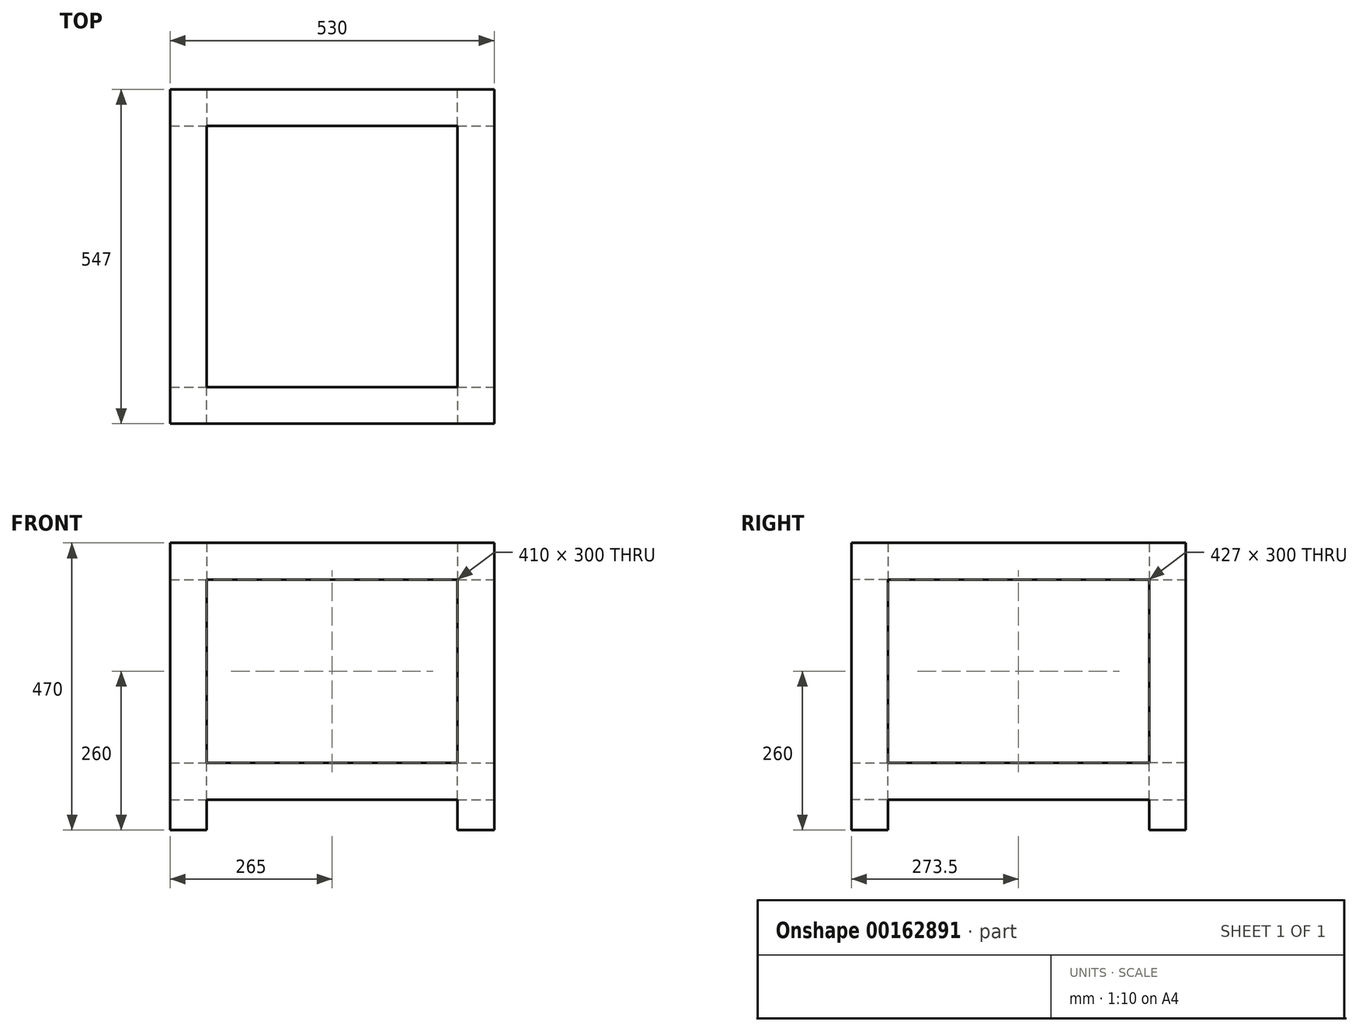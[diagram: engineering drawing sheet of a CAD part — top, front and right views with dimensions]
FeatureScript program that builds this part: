
annotation { "Feature Type Name" : "Feature", "Feature Type Description" : "" }
export const myFeature = defineFeature(function(context is Context, id is Id, definition is map)
    precondition{}
    {
        {
            var Q0;
            Q0=qCreatedBy(makeId("Top.planeOp"),FACE);
            var sketch = newSketch(context, id + "F0", { "sketchPlane" : qUnion([Q0])});
            skLineSegment(sketch, "E0.bottom", {"start": v(205, -213.5) * mm, "end": v(-205, -213.5) * mm});
            skLineSegment(sketch, "E0.top", {"start": v(205, 213.5) * mm, "end": v(-205, 213.5) * mm});
            skLineSegment(sketch, "E0.left", {"start": v(205, -213.5) * mm, "end": v(205, 213.5) * mm});
            skLineSegment(sketch, "E0.right", {"start": v(-205, -213.5) * mm, "end": v(-205, 213.5) * mm});
            skPoint(sketch, "E0.middle", {"position": v(0, 0) * mm});
            skLineSegment(sketch, "E1.bottom", {"start": v(265, -273.5) * mm, "end": v(-265, -273.5) * mm});
            skLineSegment(sketch, "E1.top", {"start": v(265, 273.5) * mm, "end": v(-265, 273.5) * mm});
            skLineSegment(sketch, "E1.left", {"start": v(265, -273.5) * mm, "end": v(265, 273.5) * mm});
            skLineSegment(sketch, "E1.right", {"start": v(-265, -273.5) * mm, "end": v(-265, 273.5) * mm});
            skSolve(sketch);
        }
        {
            var Q0;
            Q0=makeQuery(id+"F0.imprint","IMPRINT",FACE,{"disambiguationData":[TD([[makeQuery(id+"F0.imprint","IMPRINT",EDGE,{"derivedFrom":sQuery(id+"F0.wireOp",EDGE,"E0.bottom")}),1.0]])]});
            extrude(context, id + "F1", {"entities" : qUnion([Q0]), "depth" : 60 * mm, "offsetDistance" : 25 * mm});
        }
        {
            var Q0;
            Q0=makeQuery(id+"F1.opExtrude","CAP_FACE",FACE,{"disambiguationData":[OSD([sQuery(id+"F0.wireOp",EDGE,"E0.bottom"),sQuery(id+"F0.wireOp",EDGE,"E0.top"),sQuery(id+"F0.wireOp",EDGE,"E0.left"),sQuery(id+"F0.wireOp",EDGE,"E0.right"),sQuery(id+"F0.wireOp",EDGE,"E1.bottom"),sQuery(id+"F0.wireOp",EDGE,"E1.top"),sQuery(id+"F0.wireOp",EDGE,"E1.left"),sQuery(id+"F0.wireOp",EDGE,"E1.right")])],"isStart":true});
            var sketch = newSketch(context, id + "F2", { "sketchPlane" : qUnion([Q0])});
            skLineSegment(sketch, "E2.bottom", {"start": v(-265, 273.5) * mm, "end": v(-205, 273.5) * mm});
            skLineSegment(sketch, "E2.top", {"start": v(-265, 213.5) * mm, "end": v(-205, 213.5) * mm});
            skLineSegment(sketch, "E2.left", {"start": v(-265, 273.5) * mm, "end": v(-265, 213.5) * mm});
            skLineSegment(sketch, "E2.right", {"start": v(-205, 273.5) * mm, "end": v(-205, 213.5) * mm});
            skLineSegment(sketch, "E3.bottom", {"start": v(205, 213.5) * mm, "end": v(265, 213.5) * mm});
            skLineSegment(sketch, "E3.top", {"start": v(205, 273.5) * mm, "end": v(265, 273.5) * mm});
            skLineSegment(sketch, "E3.left", {"start": v(205, 213.5) * mm, "end": v(205, 273.5) * mm});
            skLineSegment(sketch, "E3.right", {"start": v(265, 213.5) * mm, "end": v(265, 273.5) * mm});
            skLineSegment(sketch, "E4.bottom", {"start": v(-265, -273.5) * mm, "end": v(-205, -273.5) * mm});
            skLineSegment(sketch, "E4.top", {"start": v(-265, -213.5) * mm, "end": v(-205, -213.5) * mm});
            skLineSegment(sketch, "E4.left", {"start": v(-265, -273.5) * mm, "end": v(-265, -213.5) * mm});
            skLineSegment(sketch, "E4.right", {"start": v(-205, -273.5) * mm, "end": v(-205, -213.5) * mm});
            skLineSegment(sketch, "E5.bottom", {"start": v(205, -213.5) * mm, "end": v(265, -213.5) * mm});
            skLineSegment(sketch, "E5.top", {"start": v(205, -273.5) * mm, "end": v(265, -273.5) * mm});
            skLineSegment(sketch, "E5.left", {"start": v(205, -213.5) * mm, "end": v(205, -273.5) * mm});
            skLineSegment(sketch, "E5.right", {"start": v(265, -213.5) * mm, "end": v(265, -273.5) * mm});
            skSolve(sketch);
        }
        {
            var Q0;
            Q0 = qSketchRegion(id + "F2", true);
            extrude(context, id + "F3", {"entities" : qUnion([Q0]), "operationType" : NewBodyOperationType.ADD, "depth" : 300 * mm, "offsetDistance" : 25 * mm});
        }
        {
            var Q0;
            Q0=makeQuery(id+"F3.opExtrude","CAP_FACE",FACE,{"disambiguationData":[OSD([sQuery(id+"F2.wireOp",EDGE,"E2.bottom"),sQuery(id+"F2.wireOp",EDGE,"E2.top"),sQuery(id+"F2.wireOp",EDGE,"E2.left"),sQuery(id+"F2.wireOp",EDGE,"E2.right")])],"isStart":false});
            var sketch = newSketch(context, id + "F4", { "sketchPlane" : qUnion([Q0])});
            skLineSegment(sketch, "E6.bottom", {"start": v(-265, 273.5) * mm, "end": v(265, 273.5) * mm});
            skLineSegment(sketch, "E6.top", {"start": v(-265, -273.5) * mm, "end": v(265, -273.5) * mm});
            skLineSegment(sketch, "E6.left", {"start": v(-265, 273.5) * mm, "end": v(-265, -273.5) * mm});
            skLineSegment(sketch, "E6.right", {"start": v(265, 273.5) * mm, "end": v(265, -273.5) * mm});
            skLineSegment(sketch, "E7.bottom", {"start": v(-205, 213.5) * mm, "end": v(205, 213.5) * mm});
            skLineSegment(sketch, "E7.top", {"start": v(-205, -213.5) * mm, "end": v(205, -213.5) * mm});
            skLineSegment(sketch, "E7.left", {"start": v(-205, 213.5) * mm, "end": v(-205, -213.5) * mm});
            skLineSegment(sketch, "E7.right", {"start": v(205, 213.5) * mm, "end": v(205, -213.5) * mm});
            skSolve(sketch);
        }
        {
            var Q0;
            Q0 = qSketchRegion(id + "F4", true);
            extrude(context, id + "F5", {"entities" : qUnion([Q0]), "operationType" : NewBodyOperationType.ADD, "depth" : 60 * mm, "offsetDistance" : 25 * mm});
        }
        {
            var Q0;
            Q0=makeQuery(id+"F5.opExtrude","CAP_FACE",FACE,{"disambiguationData":[OSD([sQuery(id+"F4.wireOp",EDGE,"E6.bottom"),sQuery(id+"F4.wireOp",EDGE,"E6.top"),sQuery(id+"F4.wireOp",EDGE,"E6.left"),sQuery(id+"F4.wireOp",EDGE,"E6.right"),sQuery(id+"F4.wireOp",EDGE,"E7.bottom"),sQuery(id+"F4.wireOp",EDGE,"E7.top"),sQuery(id+"F4.wireOp",EDGE,"E7.left"),sQuery(id+"F4.wireOp",EDGE,"E7.right")])],"isStart":false});
            var sketch = newSketch(context, id + "F6", { "sketchPlane" : qUnion([Q0])});
            skLineSegment(sketch, "E8.bottom", {"start": v(-265, 273.5) * mm, "end": v(-205, 273.5) * mm});
            skLineSegment(sketch, "E8.top", {"start": v(-265, 213.5) * mm, "end": v(-205, 213.5) * mm});
            skLineSegment(sketch, "E8.left", {"start": v(-265, 273.5) * mm, "end": v(-265, 213.5) * mm});
            skLineSegment(sketch, "E8.right", {"start": v(-205, 273.5) * mm, "end": v(-205, 213.5) * mm});
            skLineSegment(sketch, "E9.bottom", {"start": v(205, 213.5) * mm, "end": v(265, 213.5) * mm});
            skLineSegment(sketch, "E9.top", {"start": v(205, 273.5) * mm, "end": v(265, 273.5) * mm});
            skLineSegment(sketch, "E9.left", {"start": v(205, 213.5) * mm, "end": v(205, 273.5) * mm});
            skLineSegment(sketch, "E9.right", {"start": v(265, 213.5) * mm, "end": v(265, 273.5) * mm});
            skLineSegment(sketch, "E10.bottom", {"start": v(-265, -273.5) * mm, "end": v(-205, -273.5) * mm});
            skLineSegment(sketch, "E10.top", {"start": v(-265, -213.5) * mm, "end": v(-205, -213.5) * mm});
            skLineSegment(sketch, "E10.left", {"start": v(-265, -273.5) * mm, "end": v(-265, -213.5) * mm});
            skLineSegment(sketch, "E10.right", {"start": v(-205, -273.5) * mm, "end": v(-205, -213.5) * mm});
            skLineSegment(sketch, "E11.bottom", {"start": v(205, -213.5) * mm, "end": v(265, -213.5) * mm});
            skLineSegment(sketch, "E11.top", {"start": v(205, -273.5) * mm, "end": v(265, -273.5) * mm});
            skLineSegment(sketch, "E11.left", {"start": v(205, -213.5) * mm, "end": v(205, -273.5) * mm});
            skLineSegment(sketch, "E11.right", {"start": v(265, -213.5) * mm, "end": v(265, -273.5) * mm});
            skSolve(sketch);
        }
        {
            var Q0;
            Q0 = qSketchRegion(id + "F6", true);
            extrude(context, id + "F7", {"entities" : qUnion([Q0]), "operationType" : NewBodyOperationType.ADD, "depth" : 50 * mm, "offsetDistance" : 25 * mm});
        }
    });
